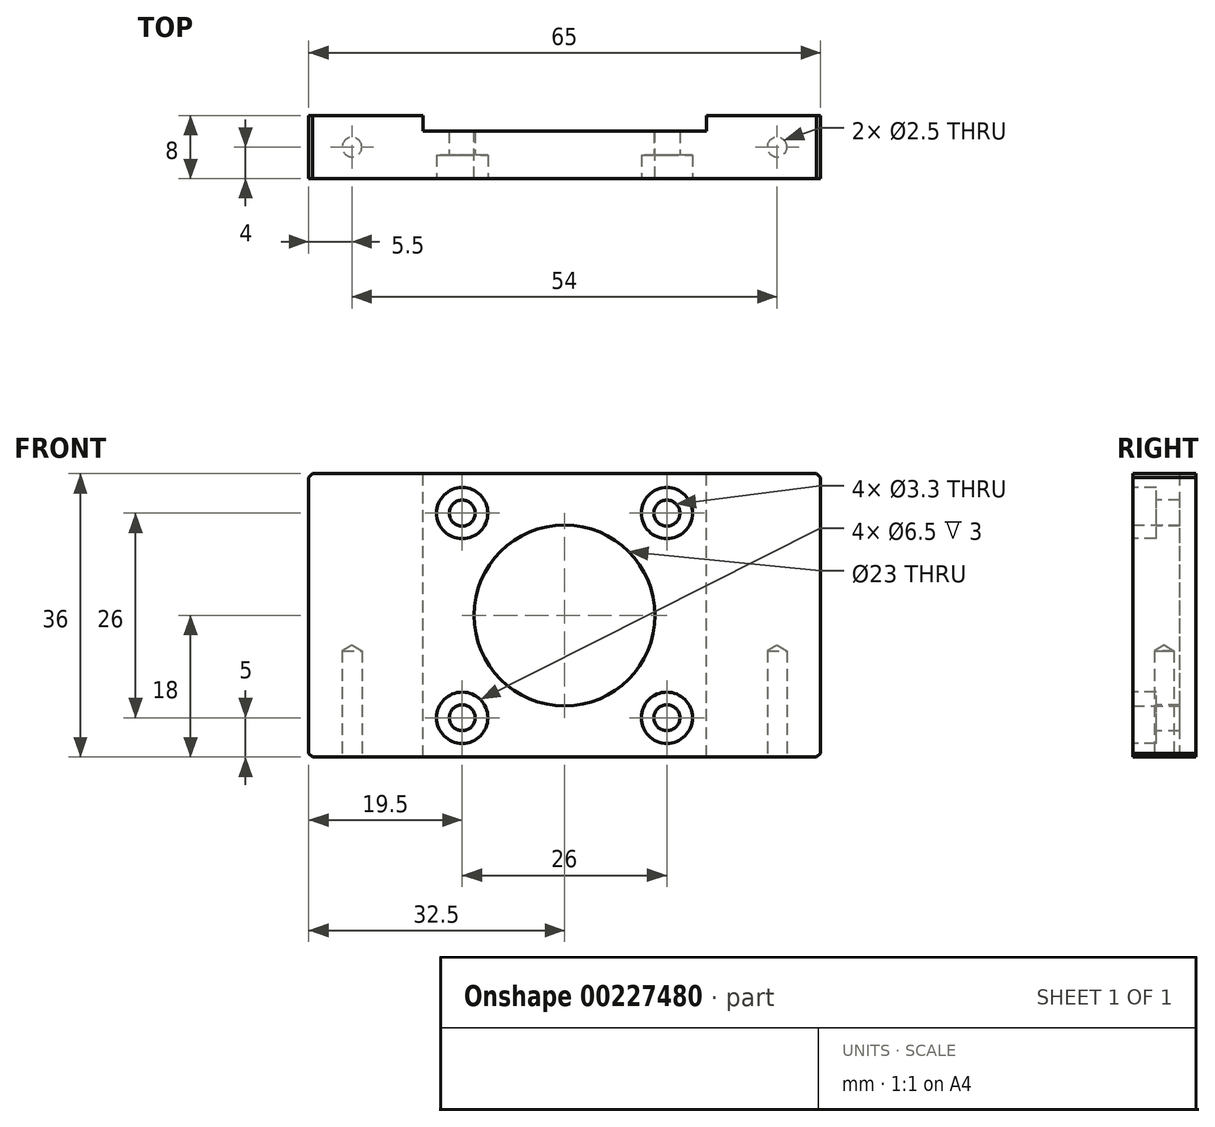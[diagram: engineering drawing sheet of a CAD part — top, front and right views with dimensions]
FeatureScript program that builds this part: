
annotation { "Feature Type Name" : "Feature", "Feature Type Description" : "" }
export const myFeature = defineFeature(function(context is Context, id is Id, definition is map)
    precondition{}
    {
        {
            var Q0;
            Q0=qCreatedBy(makeId("Front.planeOp"),FACE);
            var sketch = newSketch(context, id + "F0", { "sketchPlane" : qUnion([Q0])});
            skLineSegment(sketch, "E0.bottom", {"start": v(32.5, -18) * mm, "end": v(-32.5, -18) * mm});
            skLineSegment(sketch, "E0.top", {"start": v(32.5, 18) * mm, "end": v(-32.5, 18) * mm});
            skLineSegment(sketch, "E0.left", {"start": v(32.5, -18) * mm, "end": v(32.5, 18) * mm});
            skLineSegment(sketch, "E0.right", {"start": v(-32.5, -18) * mm, "end": v(-32.5, 18) * mm});
            skPoint(sketch, "E0.middle", {"position": v(0, 0) * mm});
            skCircle(sketch, "E1", {"center": v(0, 0) * mm, "radius": 11.5 * mm});
            skSolve(sketch);
        }
        {
            var Q0;
            Q0=makeQuery(id+"F0.imprint","IMPRINT",FACE,{"disambiguationData":[TD([[makeQuery(id+"F0.imprint","IMPRINT",EDGE,{"derivedFrom":sQuery(id+"F0.wireOp",EDGE,"E0.bottom")}),-1.0]])]});
            extrude(context, id + "F1", {"entities" : qUnion([Q0]), "depth" : 8 * mm});
        }
        {
            var Q0;
            Q0=makeQuery(id+"F1.opExtrude","CAP_FACE",FACE,{"disambiguationData":[OSD([sQuery(id+"F0.wireOp",EDGE,"E0.bottom"),sQuery(id+"F0.wireOp",EDGE,"E0.top"),sQuery(id+"F0.wireOp",EDGE,"E0.left"),sQuery(id+"F0.wireOp",EDGE,"E0.right")])],"isStart":false});
            var sketch = newSketch(context, id + "F2", { "sketchPlane" : qUnion([Q0])});
            skPoint(sketch, "E2", {"position": v(13, 13) * mm});
            skPoint(sketch, "E3.MirrorP", {"position": v(-13, 13) * mm});
            skPoint(sketch, "E4.MirrorP", {"position": v(13, -13) * mm});
            skPoint(sketch, "E5.MirrorP", {"position": v(-13, -13) * mm});
            skSolve(sketch);
        }
        {
            var Q0;
            Q0=sQuery(id+"F2.wireOp",VERTEX,"E2");
            var Q1;
            Q1=sQuery(id+"F2.wireOp",VERTEX,"E4.MirrorP");
            var Q2;
            Q2=sQuery(id+"F2.wireOp",VERTEX,"E5.MirrorP");
            var Q3;
            Q3=sQuery(id+"F2.wireOp",VERTEX,"E3.MirrorP");
            var Q4;
            Q4=makeQuery(id+"F1.opExtrude","SWEPT_BODY",BODY,{"disambiguationData":[OSD([sQuery(id+"F0.wireOp",EDGE,"E0.bottom"),sQuery(id+"F0.wireOp",EDGE,"E0.top"),sQuery(id+"F0.wireOp",EDGE,"E0.left"),sQuery(id+"F0.wireOp",EDGE,"E0.right")])]});
            hole(context, id + "F3", {"style" : HoleStyle.C_BORE, "endStyle" : HoleEndStyle.THROUGH, "standardTappedOrClearance" : lookupTablePath({ "standard" : "ISO", "fit" : "Normal", "size" : "M3", "type" : "Clearance" }), "standardBlindInLast" : lookupTablePath({ "fit" : "Standard", "standard" : "ISO", "size" : "M3", "type" : "Clearance" }), "holeDiameter" : 3.3 * mm, "cBoreDiameter" : 6.5 * mm, "cBoreDepth" : 3 * mm, "locations" : qUnion([Q0, Q1, Q2, Q3]), "scope" : qUnion([Q4]), "isTappedThrough" : true});
        }
        {
            var Q0;
            Q0=makeQuery(id+"F1.opExtrude","SWEPT_EDGE",EDGE,{"disambiguationData":[OSD([sQuery(id+"F0.wireOp",EDGE,"E0.top"),sQuery(id+"F0.wireOp",EDGE,"E0.right")])]});
            var Q1;
            Q1=makeQuery(id+"F1.opExtrude","SWEPT_EDGE",EDGE,{"disambiguationData":[OSD([sQuery(id+"F0.wireOp",EDGE,"E0.top"),sQuery(id+"F0.wireOp",EDGE,"E0.left")])]});
            var Q2;
            Q2=makeQuery(id+"F1.opExtrude","SWEPT_EDGE",EDGE,{"disambiguationData":[OSD([sQuery(id+"F0.wireOp",EDGE,"E0.bottom"),sQuery(id+"F0.wireOp",EDGE,"E0.left")])]});
            var Q3;
            Q3=makeQuery(id+"F1.opExtrude","SWEPT_EDGE",EDGE,{"disambiguationData":[OSD([sQuery(id+"F0.wireOp",EDGE,"E0.bottom"),sQuery(id+"F0.wireOp",EDGE,"E0.right")])]});
            chamfer(context, id + "F4", {"entities" : qUnion([Q0, Q1, Q2, Q3]), "width" : 0.5 * mm, "tangentPropagation" : true});
        }
        {
            var Q0;
            Q0=makeQuery(id+"F1.opExtrude","SWEPT_FACE",FACE,{"disambiguationData":[OSD([sQuery(id+"F0.wireOp",EDGE,"E0.bottom")])]});
            var sketch = newSketch(context, id + "F5", { "sketchPlane" : qUnion([Q0])});
            skPoint(sketch, "E6", {"position": v(27, 4) * mm});
            skPoint(sketch, "E7.MirrorP", {"position": v(-27, 4) * mm});
            skSolve(sketch);
        }
        {
            var Q0;
            Q0=sQuery(id+"F5.wireOp",VERTEX,"E6");
            var Q1;
            Q1=sQuery(id+"F5.wireOp",VERTEX,"E7.MirrorP");
            var Q2;
            Q2=makeQuery(id+"F1.opExtrude","SWEPT_BODY",BODY,{"disambiguationData":[OSD([sQuery(id+"F0.wireOp",EDGE,"E0.bottom"),sQuery(id+"F0.wireOp",EDGE,"E0.top"),sQuery(id+"F0.wireOp",EDGE,"E0.left"),sQuery(id+"F0.wireOp",EDGE,"E0.right"),sQuery(id+"F0.wireOp",EDGE,"E1")])]});
            hole(context, id + "F6", {"style" : HoleStyle.SIMPLE, "endStyle" : HoleEndStyle.BLIND, "standardTappedOrClearance" : lookupTablePath({ "standard" : "ISO", "engagement" : "75%", "pitch" : "0.5 mm", "size" : "M3", "type" : "Tapped" }), "standardBlindInLast" : lookupTablePath({ "standard" : "ISO", "engagement" : "75%", "pitch" : "0.5 mm", "size" : "M3", "type" : "Tapped" }), "holeDiameter" : 2.5 * mm, "holeDepth" : 13.5 * mm, "locations" : qUnion([Q0, Q1]), "scope" : qUnion([Q2]), "showTappedDepth" : true, "tappedDepth" : 12 * mm, "tapClearance" : 3, "majorDiameter" : 3 * mm});
        }
        {
            var Q0;
            Q0=makeQuery(id+"F1.opExtrude","CAP_FACE",FACE,{"disambiguationData":[OSD([sQuery(id+"F0.wireOp",EDGE,"E0.bottom"),sQuery(id+"F0.wireOp",EDGE,"E0.top"),sQuery(id+"F0.wireOp",EDGE,"E0.left"),sQuery(id+"F0.wireOp",EDGE,"E0.right"),sQuery(id+"F0.wireOp",EDGE,"E1")])],"isStart":true});
            var sketch = newSketch(context, id + "F7", { "sketchPlane" : qUnion([Q0])});
            skLineSegment(sketch, "E8.bottom", {"start": v(18, -18) * mm, "end": v(-18, -18) * mm});
            skLineSegment(sketch, "E8.top", {"start": v(18, 18) * mm, "end": v(-18, 18) * mm});
            skLineSegment(sketch, "E8.left", {"start": v(18, -18) * mm, "end": v(18, 18) * mm});
            skLineSegment(sketch, "E8.right", {"start": v(-18, -18) * mm, "end": v(-18, 18) * mm});
            skPoint(sketch, "E8.middle", {"position": v(0, 0) * mm});
            skSolve(sketch);
        }
        {
            var Q0;
            Q0=makeQuery(id+"F7.imprint","IMPRINT",FACE,{"disambiguationData":[TD([[makeQuery(id+"F7.imprint","IMPRINT",EDGE,{"derivedFrom":sQuery(id+"F7.wireOp",EDGE,"E8.bottom")}),1.0]])]});
            extrude(context, id + "F8", {"entities" : qUnion([Q0]), "operationType" : NewBodyOperationType.REMOVE, "oppositeDirection" : true, "depth" : 2 * mm});
        }
    });
